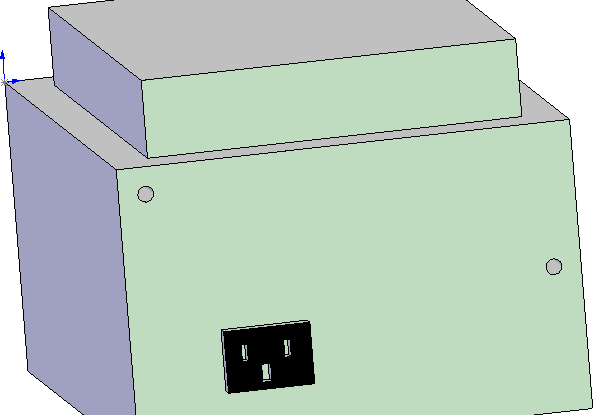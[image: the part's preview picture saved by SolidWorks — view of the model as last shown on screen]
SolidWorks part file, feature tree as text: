
SOLIDWORKS PART (.sldprt)
format: sldprt  version: not decoded by parser v0  size: 106,496 bytes
history: native  units: mm
features: sketch x5, extrude x3, cut_extrude x2 (+11 scaffold rows collapsed)
feature tree (21):
  scaffold x11  (default folders/planes/origin — collapsed)
  sketch  "Sketch1"  dims[D1=100.0mm D2=63.5mm]
  extrude  "Extrude1"  Depth=125mm
  sketch  "Sketch2"
  extrude  "Extrude2"  Depth=17.1mm
  sketch  "Sketch3"  dims[D1=3.51mm D2=3.51mm D3=3.51mm D4=6.0mm D5=31.8mm D6=6.0mm D7=6.0mm D8=6.0mm D9=6.0mm]
  cut_extrude  "Cut-Extrude1"  Depth=17.1mm
  sketch  "Sketch4"
  extrude  "Extrude3"  Depth=3mm
  sketch  "Sketch5"
  cut_extrude  "Cut-Extrude2"  Depth=3mm
decode coverage: 7 of 10 modeling features carry decoded parameters
note: suppression state not decoded; provenance and decode notes live in map.json
